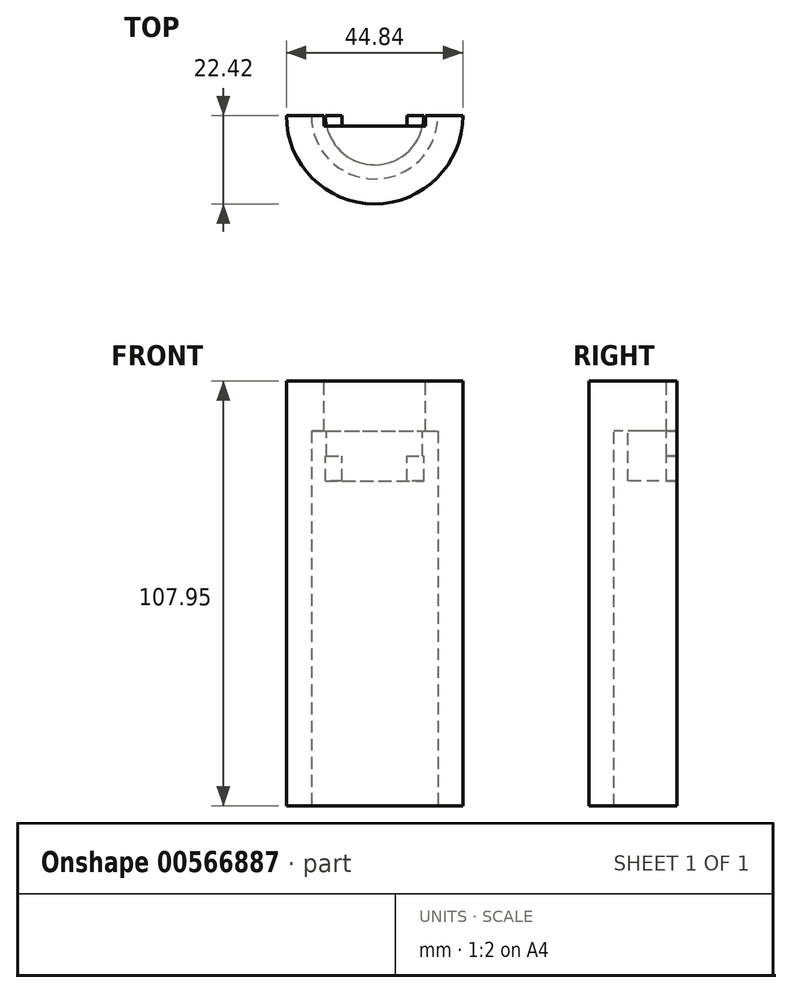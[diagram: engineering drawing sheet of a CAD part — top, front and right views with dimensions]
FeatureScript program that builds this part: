
annotation { "Feature Type Name" : "Feature", "Feature Type Description" : "" }
export const myFeature = defineFeature(function(context is Context, id is Id, definition is map)
    precondition{}
    {
        {
            var Q0;
            Q0=qCreatedBy(makeId("Front.planeOp"),FACE);
            var sketch = newSketch(context, id + "F0", { "sketchPlane" : qUnion([Q0])});
            skLineSegment(sketch, "E0", {"start": v(16.07, -98.6) * mm, "end": v(22.42, -98.6) * mm});
            skLineSegment(sketch, "E1", {"start": v(22.42, -98.6) * mm, "end": v(22.42, 9.36) * mm});
            skLineSegment(sketch, "E2", {"start": v(22.42, 9.36) * mm, "end": v(0, 9.36) * mm});
            skLineSegment(sketch, "E3", {"start": v(0, 9.36) * mm, "end": v(0, -16.04) * mm});
            skLineSegment(sketch, "E4", {"start": v(0, -16.04) * mm, "end": v(12.5, -16.04) * mm});
            skLineSegment(sketch, "E5", {"start": v(12.5, -16.04) * mm, "end": v(12.5, -3.34) * mm});
            skLineSegment(sketch, "E6", {"start": v(12.5, -3.34) * mm, "end": v(16.07, -3.34) * mm});
            skLineSegment(sketch, "E7", {"start": v(16.07, -3.34) * mm, "end": v(16.07, -98.6) * mm});
            skSolve(sketch);
        }
        {
            var Q0;
            Q0=makeQuery(id+"F0.imprint","IMPRINT",FACE,{"disambiguationData":[TD([[makeQuery(id+"F0.imprint","IMPRINT",EDGE,{"derivedFrom":sQuery(id+"F0.wireOp",EDGE,"E0")}),1.0]])]});
            var Q1;
            Q1=sQuery(id+"F0.wireOp",EDGE,"E3");
            revolve(context, id + "F1", {"entities" : qUnion([Q0]), "axis" : qUnion([Q1]), "revolveType" : RevolveType.ONE_DIRECTION, "angle" : 180 * degree});
        }
        {
            var Q0;
            Q0=makeQuery(id+"F1.opRevolve","SWEPT_FACE",FACE,{"disambiguationData":[OSD([sQuery(id+"F0.wireOp",EDGE,"E2")])]});
            var sketch = newSketch(context, id + "F2", { "sketchPlane" : qUnion([Q0])});
            skLineSegment(sketch, "E8.bottom", {"start": v(8.26, 2.67) * mm, "end": v(-8.26, 2.67) * mm});
            skLineSegment(sketch, "E8.top", {"start": v(8.26, -2.67) * mm, "end": v(-8.26, -2.67) * mm});
            skLineSegment(sketch, "E8.left", {"start": v(8.26, 2.67) * mm, "end": v(8.25, -2.67) * mm});
            skLineSegment(sketch, "E8.right", {"start": v(-8.26, 2.67) * mm, "end": v(-8.26, -2.67) * mm});
            skPoint(sketch, "E8.middle", {"position": v(0, 0) * mm});
            skLineSegment(sketch, "E9.bottom", {"start": v(-12.9, -2.67) * mm, "end": v(12.9, -2.67) * mm});
            skLineSegment(sketch, "E9.top", {"start": v(-12.9, 2.67) * mm, "end": v(12.9, 2.67) * mm});
            skLineSegment(sketch, "E9.left", {"start": v(-12.9, -2.67) * mm, "end": v(-12.9, 2.67) * mm});
            skLineSegment(sketch, "E9.right", {"start": v(12.9, -2.67) * mm, "end": v(12.9, 2.67) * mm});
            skSolve(sketch);
        }
        {
            var Q0;
            {var subQ0=sQuery(id+"F2.wireOp",EDGE,"E9.bottom");var subQ1=sQuery(id+"F2.wireOp",EDGE,"E8.left");var subQ2=makeQuery(id+"F2.imprint","INTERSECT",VERTEX,{"derivedFrom":[subQ1,subQ0]});Q0=makeQuery(id+"F2.imprint","IMPRINT",FACE,{"disambiguationData":[TD([[makeQuery(id+"F2.imprint","IMPRINT",EDGE,{"disambiguationData":[TD([[subQ2,1.0]])],"derivedFrom":subQ1}),-1.0]])]});}
            var Q1;
            Q1=makeQuery(id+"F1.opRevolve","SWEPT_FACE",FACE,{"disambiguationData":[OSD([sQuery(id+"F0.wireOp",EDGE,"E4")])]});
            extrude(context, id + "F3", {"entities" : qUnion([Q0]), "operationType" : NewBodyOperationType.REMOVE, "endBound" : BoundingType.UP_TO_SURFACE, "oppositeDirection" : true, "depth" : 47.24 * mm, "endBoundEntityFace" : qUnion([Q1]), "offsetDistance" : 25.4 * mm});
        }
        {
            var Q0;
            {var subQ0=sQuery(id+"F2.wireOp",EDGE,"E9.bottom");var subQ1=sQuery(id+"F2.wireOp",EDGE,"E8.left");var subQ2=makeQuery(id+"F2.imprint","INTERSECT",VERTEX,{"derivedFrom":[subQ1,subQ0]});Q0=makeQuery(id+"F2.imprint","IMPRINT",FACE,{"disambiguationData":[TD([[makeQuery(id+"F2.imprint","IMPRINT",EDGE,{"disambiguationData":[TD([[subQ2,1.0]])],"derivedFrom":subQ1}),1.0]])]});}
            var Q1;
            {var subQ0=sQuery(id+"F2.wireOp",EDGE,"E9.bottom");var subQ1=sQuery(id+"F2.wireOp",EDGE,"E8.right");var subQ2=makeQuery(id+"F2.imprint","INTERSECT",VERTEX,{"derivedFrom":[subQ1,subQ0]});Q1=makeQuery(id+"F2.imprint","IMPRINT",FACE,{"disambiguationData":[TD([[makeQuery(id+"F2.imprint","IMPRINT",EDGE,{"disambiguationData":[TD([[subQ2,1.0]])],"derivedFrom":subQ1}),-1.0]])]});}
            extrude(context, id + "F4", {"entities" : qUnion([Q0, Q1]), "operationType" : NewBodyOperationType.REMOVE, "oppositeDirection" : true, "depth" : 19.05 * mm, "offsetDistance" : 25.4 * mm});
        }
    });
